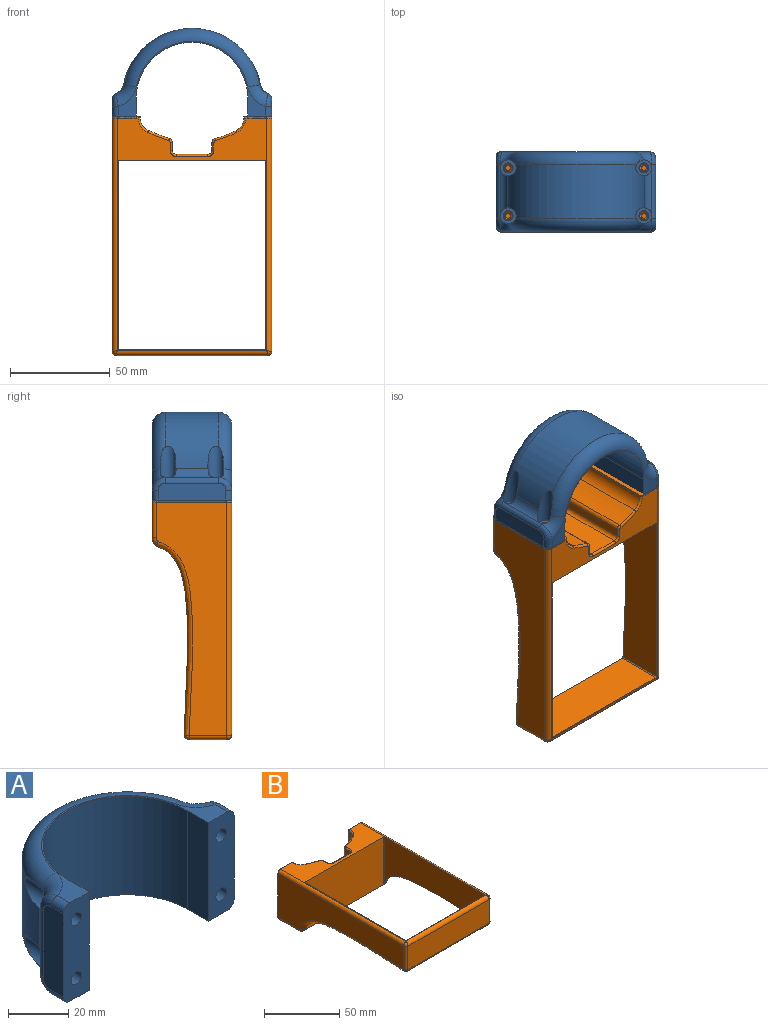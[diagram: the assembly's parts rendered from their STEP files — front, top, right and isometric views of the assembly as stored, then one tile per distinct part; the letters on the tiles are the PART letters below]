
ASSEMBLY  parts=2 mates=1
PART A: 40 faces, bbox 80x47.9x40.1 mm
  f0: cylinder r=35mm len=68.66mm, axis (0,0,-1), area 2363.2mm2, adj f10,f12,f14,f16,f22,f23,f25,f28
  f1: cylinder r=28mm len=56mm, axis (0,0,-1), area 3518.6mm2, adj f2,f7,f8,f9
  f2: plane 40x10mm, normal (-1,0,0), area 400mm2, adj f1,f3,f8,f9
  f3: plane 40x12mm, normal (0,-1,0), area 436.9mm2, adj f2,f4,f8,f9,f18,f19,f35,f39
  f4: plane 34x9.59mm, normal (1,0,0), area 320.5mm2, adj f3,f35,f36,f37,f38,f39
  f5: plane 34x9.59mm, normal (-1,0,0), area 320.5mm2, adj f6,f30,f31,f32,f33,f34
  f6: plane 40x12mm, normal (0,-1,0), area 436.9mm2, adj f5,f7,f8,f9,f20,f21,f30,f34
  f7: plane 40x10mm, normal (1,0,0), area 400mm2, adj f1,f6,f8,f9
  f8: plane 74x38.5mm, normal (0,0,1), area 199.8mm2, adj f1,f2,f3,f6,f7,f24,f25,f26
  f9: plane 74x38.5mm, normal (0,0,-1), area 199.8mm2, adj f1,f2,f3,f6,f7,f27,f28,f29
  f10: cylinder r=4mm len=19.23mm, axis (0,1,0), area 258.7mm2, adj f0,f11,f23,f27,f28
  f11: plane 8x8mm, normal (0,1,0), area 30.6mm2, adj f10,f21
  f12: cylinder r=4mm len=19.23mm, axis (0,1,0), area 258.6mm2, adj f0,f13,f23,f24,f25
  f13: plane 8x8mm, normal (0,1,0), area 30.6mm2, adj f12,f20
  f14: cylinder r=4mm len=19.23mm, axis (0,1,0), area 258.7mm2, adj f0,f15,f22,f25,f26
  f15: plane 8x8mm, normal (0,1,0), area 30.6mm2, adj f14,f19
  f16: cylinder r=4mm len=19.23mm, axis (0,1,0), area 258.6mm2, adj f0,f17,f22,f28,f29
  f17: plane 8x8mm, normal (0,1,0), area 30.6mm2, adj f16,f18
  f18: cylinder r=2.5mm len=8.8mm, axis (0,1,0), area 138.2mm2, adj f3,f17
  f19: cylinder r=2.5mm len=8.8mm, axis (0,1,0), area 138.2mm2, adj f3,f15
  f20: cylinder r=2.5mm len=8.8mm, axis (0,1,0), area 138.2mm2, adj f6,f13
  f21: cylinder r=2.5mm len=8.8mm, axis (0,1,0), area 138.2mm2, adj f6,f11
  f22: cylinder r=6mm len=27mm, axis (0,0,1), area 106.4mm2, adj f0,f14,f16,f26,f29,f37
  f23: cylinder r=6mm len=27mm, axis (0,0,1), area 106.4mm2, adj f0,f10,f12,f24,f27,f32
  f24: torus R=12.5mm, axis (0,0,1), area 78.7mm2, adj f8,f12,f23,f25,f33
  f25: torus R=28.5mm, axis (0,0,1), area 871.3mm2, adj f0,f8,f12,f14,f24,f26
  f26: torus R=12.5mm, axis (0,0,1), area 78.7mm2, adj f8,f14,f22,f25,f38
  f27: torus R=12.5mm, axis (0,0,1), area 78.7mm2, adj f9,f10,f23,f28,f31
  f28: torus R=28.5mm, axis (0,0,1), area 871.3mm2, adj f0,f9,f10,f16,f27,f29
  f29: torus R=12.5mm, axis (0,0,1), area 78.7mm2, adj f9,f16,f22,f28,f36
  f30: cylinder r=3mm len=5.92mm, axis (0,-1,0), area 27.9mm2, adj f5,f6,f9,f31
  f31: bspline ~7.99x7.95mm, area 34mm2, adj f5,f27,f30,f32
  f32: cylinder r=3mm len=27mm, axis (0,0,1), area 97.7mm2, adj f5,f23,f31,f33
  f33: bspline ~7.92x6.85mm, area 34mm2, adj f5,f24,f32,f34
  f34: cylinder r=3mm len=5.92mm, axis (0,1,0), area 27.9mm2, adj f5,f6,f8,f33
  f35: cylinder r=3mm len=5.92mm, axis (0,1,0), area 27.9mm2, adj f3,f4,f9,f36
  f36: bspline ~7.92x6.85mm, area 34mm2, adj f4,f29,f35,f37
  f37: cylinder r=3mm len=27mm, axis (0,0,1), area 97.7mm2, adj f4,f22,f36,f38
  f38: bspline ~7.99x7.95mm, area 34mm2, adj f4,f26,f37,f39
  f39: cylinder r=3mm len=5.92mm, axis (0,-1,0), area 27.9mm2, adj f3,f4,f8,f38
PART B: 90 faces, bbox 80.1x119.8x40.4 mm
  f0: cylinder r=5mm len=1.18mm, axis (1,0,0), area 0.2mm2, adj f5,f70,f85
  f1: plane 27.49x18.6mm, normal (0,0,-1), area 360.4mm2, adj f9,f39,f40,f41,f42,f43,f44,f86
  f2: plane 24.49x18.6mm, normal (0,0,-1), area 301.6mm2, adj f13,f32,f33,f34,f35,f36,f37,f84
  f3: plane 94.91x38.19mm, normal (1,0,0), area 2244.4mm2, adj f19,f26,f29,f70,f86
  f4: plane 73.1x38.71mm, normal (0,-1,0), area 2829.6mm2, adj f19,f26,f27,f86
  f5: plane 94.92x38.19mm, normal (-1,0,0), area 2244.4mm2, adj f0,f19,f27,f28,f70,f85
  f6: plane 38x4.04mm, normal (1,0,0), area 153.4mm2, adj f21,f24,f40,f49
  f7: cylinder r=101.57mm len=38mm, axis (0,0,-1), area 428.2mm2, adj f22,f24,f42,f47
  f8: plane 38x0.57mm, normal (1,0,0), area 21.8mm2, adj f9,f22,f44,f45
  f9: plane 40x14mm, normal (0,1,0), area 531mm2, adj f1,f8,f10,f19,f44,f45,f68,f69
  f10: plane 117.77x35.5mm, normal (-1,0,0), area 2581.6mm2, adj f9,f30,f75,f79,f82,f87,f88
  f11: plane 76x18.94mm, normal (0,-1,0), area 1439.1mm2, adj f30,f31,f73,f80
  f12: plane 117.76x32.5mm, normal (1,0,0), area 2519.7mm2, adj f13,f31,f71,f76,f77,f84
  f13: plane 40x14mm, normal (0,1,0), area 526.5mm2, adj f2,f12,f14,f19,f32,f57,f66,f67
  f14: plane 38x0.76mm, normal (-1,0,0), area 28.9mm2, adj f13,f23,f32,f57
  f15: cylinder r=63.81mm len=38mm, axis (0,0,-1), area 430.7mm2, adj f23,f25,f34,f55
  f16: plane 38x3.96mm, normal (-1,0,0), area 150.6mm2, adj f20,f25,f36,f53
  f17: plane 38x16mm, normal (0,1,0), area 608mm2, adj f20,f21,f38,f51
  f18: plane 73.1x23.92mm, normal (0,1,0), area 1748.5mm2, adj f19,f28,f29,f70
  f19: plane 117.26x75mm, normal (0,0,1), area 1047.3mm2, adj f3,f4,f5,f9,f13,f18,f26,f27
  f20: cylinder r=2mm len=38mm, axis (0,0,1), area 119.4mm2, adj f16,f17,f37,f52
  f21: cylinder r=2mm len=38mm, axis (0,0,1), area 119.4mm2, adj f6,f17,f39,f50
  f22: cylinder r=7mm len=38mm, axis (0,0,-1), area 304.8mm2, adj f7,f8,f43,f46
  f23: cylinder r=7mm len=38mm, axis (0,0,-1), area 298mm2, adj f14,f15,f33,f56
  f24: cylinder r=2mm len=38mm, axis (0,0,-1), area 95.5mm2, adj f6,f7,f41,f48
  f25: cylinder r=2mm len=38mm, axis (0,0,-1), area 98.6mm2, adj f15,f16,f35,f54
  f26: cylinder r=0.5mm len=38.71mm, axis (0,0,-1), area 30.2mm2, adj f3,f4,f19,f86
  f27: cylinder r=0.5mm len=38.71mm, axis (0,0,1), area 30.2mm2, adj f4,f5,f19,f85,f86
  f28: cylinder r=0.5mm len=23.92mm, axis (0,0,-1), area 18.8mm2, adj f5,f18,f19,f70
  f29: cylinder r=0.5mm len=23.92mm, axis (0,0,1), area 18.8mm2, adj f3,f18,f19,f70
  f30: cylinder r=2mm len=18.94mm, axis (0,0,1), area 59.5mm2, adj f10,f11,f74,f82
  f31: cylinder r=2mm len=18.94mm, axis (0,0,-1), area 59.5mm2, adj f11,f12,f72,f77
  f32: cylinder r=1mm len=1mm, axis (0,-1,0), area 1.2mm2, adj f2,f13,f14,f33
  f33: torus R=8mm, axis (0,0,1), area 13mm2, adj f2,f23,f32,f34
  f34: torus R=64.81mm, axis (0,0,1), area 17.9mm2, adj f2,f15,f33,f35
  f35: torus R=1mm, axis (0,0,1), area 3.3mm2, adj f2,f25,f34,f36
  f36: cylinder r=1mm len=3.96mm, axis (0,-1,0), area 6.2mm2, adj f2,f16,f35,f37
  f37: torus R=3mm, axis (0,0,1), area 5.2mm2, adj f2,f20,f36,f38,f86
  f38: cylinder r=1mm len=16mm, axis (-1,0,0), area 18.3mm2, adj f17,f37,f39,f86
  f39: torus R=3mm, axis (0,0,1), area 5.2mm2, adj f1,f21,f38,f40,f86
  f40: cylinder r=1mm len=4.04mm, axis (0,1,0), area 6.3mm2, adj f1,f6,f39,f41
  f41: torus R=1mm, axis (0,0,1), area 3.2mm2, adj f1,f24,f40,f42
  f42: torus R=102.57mm, axis (0,0,1), area 17.8mm2, adj f1,f7,f41,f43
  f43: torus R=8mm, axis (0,0,1), area 13.3mm2, adj f1,f22,f42,f44
  f44: cylinder r=1mm len=1mm, axis (0,1,0), area 0.9mm2, adj f1,f8,f9,f43
  f45: cylinder r=1mm len=1mm, axis (0,-1,0), area 0.9mm2, adj f8,f9,f19,f46
  f46: torus R=8mm, axis (0,0,1), area 13.3mm2, adj f19,f22,f45,f47
  f47: torus R=102.57mm, axis (0,0,1), area 17.8mm2, adj f7,f19,f46,f48
  f48: torus R=1mm, axis (0,0,1), area 3.2mm2, adj f19,f24,f47,f49
  f49: cylinder r=1mm len=4.04mm, axis (0,-1,0), area 6.3mm2, adj f6,f19,f48,f50
  f50: torus R=3mm, axis (0,0,1), area 5.8mm2, adj f19,f21,f49,f51
  f51: cylinder r=1mm len=16mm, axis (1,0,0), area 25.1mm2, adj f17,f19,f50,f52
  f52: torus R=3mm, axis (0,0,1), area 5.8mm2, adj f19,f20,f51,f53
  f53: cylinder r=1mm len=3.96mm, axis (0,1,0), area 6.2mm2, adj f16,f19,f52,f54
  f54: torus R=1mm, axis (0,0,1), area 3.3mm2, adj f19,f25,f53,f55
  f55: torus R=64.81mm, axis (0,0,1), area 17.9mm2, adj f15,f19,f54,f56
  f56: torus R=8mm, axis (0,0,1), area 13mm2, adj f19,f23,f55,f57
  f57: cylinder r=1mm len=1mm, axis (0,1,0), area 1.2mm2, adj f13,f14,f19,f56
  f58: cylinder r=1.25mm len=17.2mm, axis (0,1,0), area 135.1mm2, adj f59,f66
  f59: plane 2.5x2.5mm, normal (0,1,0), area 4.9mm2, adj f58
  f60: cylinder r=1.25mm len=17.2mm, axis (0,1,0), area 135.1mm2, adj f61,f67
  f61: plane 2.5x2.5mm, normal (0,1,0), area 4.9mm2, adj f60
  f62: cylinder r=1.25mm len=17.2mm, axis (0,1,0), area 135.1mm2, adj f63,f68
  f63: plane 2.5x2.5mm, normal (0,1,0), area 4.9mm2, adj f62
  f64: cylinder r=1.25mm len=17.2mm, axis (0,1,0), area 135.1mm2, adj f65,f69
  f65: plane 2.5x2.5mm, normal (0,1,0), area 4.9mm2, adj f64
  f66: cone r=1.25mm half-angle=45deg, axis (0,1,0), area 11.7mm2, adj f13,f58
  f67: cone r=1.25mm half-angle=45deg, axis (0,1,0), area 11.7mm2, adj f13,f60
  f68: cone r=1.25mm half-angle=45deg, axis (0,1,0), area 11.7mm2, adj f9,f62
  f69: cone r=1.25mm half-angle=45deg, axis (0,1,0), area 11.7mm2, adj f9,f64
  f70: extruded ~93.86x75mm, area 120mm2, adj f0,f3,f5,f18,f28,f29,f76,f79
  f71: cylinder r=2.5mm len=117.76mm, axis (0,-1,0), area 461.5mm2, adj f12,f13,f19,f72
  f72: bspline ~2.65x2.5mm, area 5.5mm2, adj f31,f71,f73
  f73: cylinder r=2.5mm len=76mm, axis (-1,0,0), area 296.5mm2, adj f11,f19,f72,f74
  f74: bspline ~2.65x2.5mm, area 5.5mm2, adj f30,f73,f75
  f75: cylinder r=2.5mm len=117.76mm, axis (0,1,0), area 461.5mm2, adj f9,f10,f19,f74
  f76: bspline ~98.52x17mm, area 391.1mm2, adj f12,f70,f78,f83
  f77: torus R=0.5mm, axis (-1,0,0), area 0.2mm2, adj f12,f31,f78,f80
  f78: bspline ~3.2x2.59mm, area 5.8mm2, adj f76,f77,f80
  f79: bspline ~99.11x18.72mm, area 397.2mm2, adj f10,f70,f81,f89
  f80: cylinder r=2.5mm len=76mm, axis (1,0,0), area 303.6mm2, adj f11,f70,f77,f78,f81,f82
  f81: bspline ~2.62x2.59mm, area 5.8mm2, adj f79,f80,f82
  f82: torus R=0.5mm, axis (-1,0,0), area 0.2mm2, adj f10,f30,f80,f81
  f83: bspline ~3.82x3.16mm, area 5.1mm2, adj f70,f76,f84,f85
  f84: cylinder r=5mm len=21.28mm, axis (0,1,0), area 157.7mm2, adj f2,f12,f13,f83,f85
  f85: bspline ~4.83x4.83mm, area 13.1mm2, adj f0,f5,f27,f83,f84,f86
  f86: cylinder r=5mm len=74.69mm, axis (1,0,0), area 254.9mm2, adj f1,f2,f3,f4,f26,f27,f37,f38
  f87: cylinder r=2mm len=18.6mm, axis (0,-1,0), area 58.4mm2, adj f1,f9,f10,f88
  f88: torus R=3mm, axis (-1,0,0), area 9.1mm2, adj f10,f86,f87,f89
  f89: bspline ~2.82x2.5mm, area 3.5mm2, adj f79,f86,f88
PLACE A rot(axis=(1,0,0),90deg) t=(11.39,56.86,13.16)mm
PLACE B rot(axis=(1,0,0),90deg) t=(43.27,56.86,-12.83)mm
MATE slider A.f16 <-> B.f66  axis (0,0,-1) through (73.39,48.86,1.16)mm
